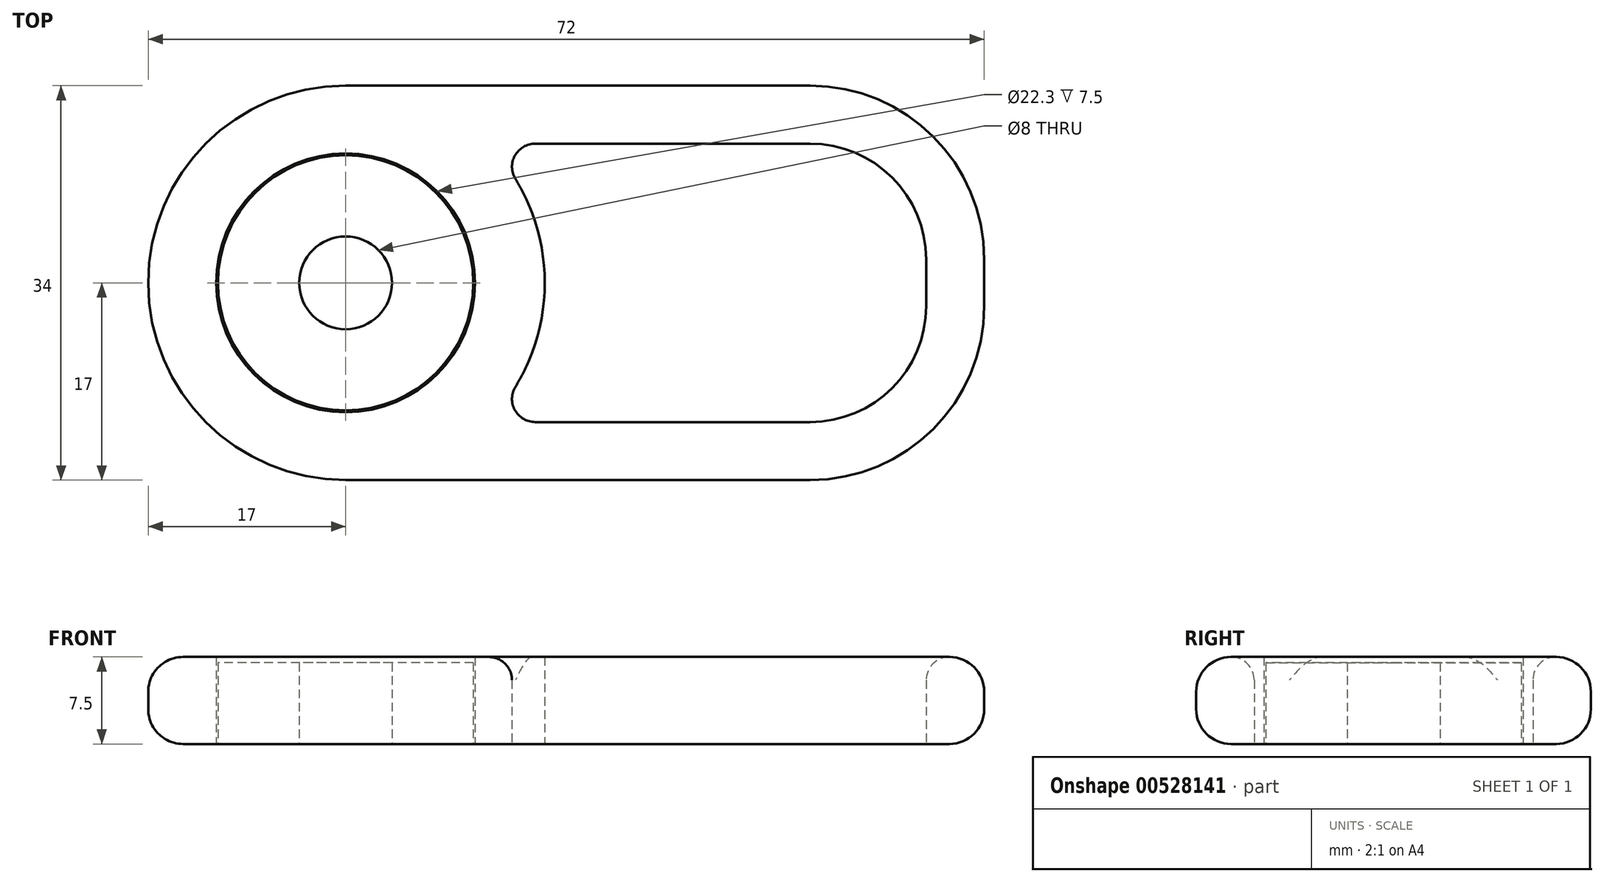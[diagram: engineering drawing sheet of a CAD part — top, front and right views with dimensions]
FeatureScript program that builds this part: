
annotation { "Feature Type Name" : "Feature", "Feature Type Description" : "" }
export const myFeature = defineFeature(function(context is Context, id is Id, definition is map)
    precondition{}
    {
        {
            var Q0;
            Q0=qCreatedBy(makeId("Top.planeOp"),FACE);
            var sketch = newSketch(context, id + "F0", { "sketchPlane" : qUnion([Q0])});
            skCircle(sketch, "E0", {"center": v(0, 0) * mm, "radius": 11 * mm});
            skCircle(sketch, "E1", {"center": v(0, 0) * mm, "radius": 4 * mm});
            skSolve(sketch);
        }
        {
            var Q0;
            Q0=makeQuery(id+"F0.imprint","IMPRINT",FACE,{"disambiguationData":[TD([[makeQuery(id+"F0.imprint","IMPRINT",EDGE,{"derivedFrom":sQuery(id+"F0.wireOp",EDGE,"E0")}),1.0]])]});
            extrude(context, id + "F1", {"entities" : qUnion([Q0]), "depth" : 7 * mm, "offsetDistance" : 25 * mm});
        }
        {
            var Q0;
            Q0=qCreatedBy(makeId("Top.planeOp"),FACE);
            var sketch = newSketch(context, id + "F2", { "sketchPlane" : qUnion([Q0])});
            skArc(sketch, "E2.0", {"start": v(0, 17) * mm, "mid": v(-17, 0) * mm, "end": v(0, -17) * mm});
            skLineSegment(sketch, "E3.bottom", {"start": v(40, -17) * mm, "end": v(0, -17) * mm});
            skLineSegment(sketch, "E3.top", {"start": v(40, 17) * mm, "end": v(0, 17) * mm});
            skLineSegment(sketch, "E3.left", {"start": v(55, -2) * mm, "end": v(55, 2) * mm});
            skPoint(sketch, "E4.visualSharp", {"position": v(55, 17) * mm});
            skArc(sketch, "E4.filletArc", {"start": v(55, 2) * mm, "mid": v(50.6, 12.6) * mm, "end": v(40, 17) * mm});
            skPoint(sketch, "E5.visualSharp", {"position": v(55, -17) * mm});
            skArc(sketch, "E5.filletArc", {"start": v(40, -17) * mm, "mid": v(50.6, -12.6) * mm, "end": v(55, -2) * mm});
            skCircle(sketch, "E6.0", {"center": v(0, 0) * mm, "radius": 11.15 * mm});
            skSolve(sketch);
        }
        {
            var Q0;
            Q0=makeQuery(id+"F2.imprint","IMPRINT",FACE,{"disambiguationData":[TD([[makeQuery(id+"F2.imprint","IMPRINT",EDGE,{"derivedFrom":sQuery(id+"F2.wireOp",EDGE,"E2.0")}),1.0]])]});
            extrude(context, id + "F3", {"entities" : qUnion([Q0]), "depth" : 7.5 * mm, "offsetDistance" : 25 * mm});
        }
        {
            var Q0;
            Q0=makeQuery(id+"F3.opExtrude","CAP_EDGE",EDGE,{"disambiguationData":[OSD([sQuery(id+"F2.wireOp",EDGE,"E3.bottom")])],"isStart":false});
            var Q1;
            Q1=makeQuery(id+"F3.opExtrude","CAP_EDGE",EDGE,{"disambiguationData":[OSD([sQuery(id+"F2.wireOp",EDGE,"E5.filletArc")])],"isStart":false});
            var Q2;
            Q2=makeQuery(id+"F3.opExtrude","CAP_EDGE",EDGE,{"disambiguationData":[OSD([sQuery(id+"F2.wireOp",EDGE,"E3.bottom")])],"isStart":true});
            fillet(context, id + "F4", {"entities" : qUnion([Q0, Q1, Q2]), "radius" : 3 * mm, "tangentPropagation" : true, "allowEdgeOverflow" : false});
        }
        {
            var Q0;
            Q0=makeQuery(id+"F3.opExtrude","CAP_FACE",FACE,{"disambiguationData":[OSD([sQuery(id+"F2.wireOp",EDGE,"E2.0"),sQuery(id+"F2.wireOp",EDGE,"E3.bottom"),sQuery(id+"F2.wireOp",EDGE,"E3.top"),sQuery(id+"F2.wireOp",EDGE,"E3.left"),sQuery(id+"F2.wireOp",EDGE,"E4.filletArc"),sQuery(id+"F2.wireOp",EDGE,"E5.filletArc"),sQuery(id+"F2.wireOp",EDGE,"E6.0")])],"isStart":true});
            var sketch = newSketch(context, id + "F5", { "sketchPlane" : qUnion([Q0])});
            skLineSegment(sketch, "E7.0", {"start": v(40, 12) * mm, "end": v(12.25, 12) * mm});
            skLineSegment(sketch, "E7.1", {"start": v(12.25, -12) * mm, "end": v(40, -12) * mm});
            skArc(sketch, "E7.2", {"start": v(40, -12) * mm, "mid": v(47.07, -9.07) * mm, "end": v(50, -2) * mm});
            skLineSegment(sketch, "E7.3", {"start": v(50, -2) * mm, "end": v(50, 2) * mm});
            skArc(sketch, "E7.4", {"start": v(50, 2) * mm, "mid": v(47.07, 9.07) * mm, "end": v(40, 12) * mm});
            skArc(sketch, "E8.0", {"start": v(12.25, -12) * mm, "mid": v(17.15, 0) * mm, "end": v(12.25, 12) * mm});
            skSolve(sketch);
        }
        {
            var Q0;
            Q0=makeQuery(id+"F5.imprint","IMPRINT",FACE,{"disambiguationData":[TD([[makeQuery(id+"F5.imprint","IMPRINT",EDGE,{"derivedFrom":sQuery(id+"F5.wireOp",EDGE,"E7.0")}),1.0]])]});
            extrude(context, id + "F6", {"entities" : qUnion([Q0]), "operationType" : NewBodyOperationType.REMOVE, "oppositeDirection" : true, "depth" : 25 * mm, "offsetDistance" : 25 * mm});
        }
        {
            var Q0;
            Q0=makeQuery(id+"F6.boolean.opBoolean","COPY",EDGE,{"derivedFrom":makeQuery(id+"F6.opExtrude","CAP_EDGE",EDGE,{"disambiguationData":[OSD([sQuery(id+"F5.wireOp",EDGE,"E7.0")])],"isStart":true})});
            var Q1;
            Q1=makeQuery(id+"F6.boolean.opBoolean","COPY",EDGE,{"derivedFrom":makeQuery(id+"F6.opExtrude","SWEPT_EDGE",EDGE,{"disambiguationData":[OSD([sQuery(id+"F5.wireOp",EDGE,"E7.0"),sQuery(id+"F5.wireOp",EDGE,"E8.0")])]})});
            var Q2;
            Q2=makeQuery(id+"F6.boolean.opBoolean","INTERSECT",EDGE,{"derivedFrom":[makeQuery(id+"F3.opExtrude","CAP_FACE",FACE,{"disambiguationData":[OSD([sQuery(id+"F2.wireOp",EDGE,"E2.0"),sQuery(id+"F2.wireOp",EDGE,"E3.bottom"),sQuery(id+"F2.wireOp",EDGE,"E3.top"),sQuery(id+"F2.wireOp",EDGE,"E3.left"),sQuery(id+"F2.wireOp",EDGE,"E4.filletArc"),sQuery(id+"F2.wireOp",EDGE,"E5.filletArc"),sQuery(id+"F2.wireOp",EDGE,"E6.0")])],"isStart":false}),makeQuery(id+"F6.opExtrude","SWEPT_FACE",FACE,{"disambiguationData":[OSD([sQuery(id+"F5.wireOp",EDGE,"E7.4")])]})]});
            var Q3;
            Q3=makeQuery(id+"F6.boolean.opBoolean","INTERSECT",EDGE,{"derivedFrom":[makeQuery(id+"F3.opExtrude","CAP_FACE",FACE,{"disambiguationData":[OSD([sQuery(id+"F2.wireOp",EDGE,"E2.0"),sQuery(id+"F2.wireOp",EDGE,"E3.bottom"),sQuery(id+"F2.wireOp",EDGE,"E3.top"),sQuery(id+"F2.wireOp",EDGE,"E3.left"),sQuery(id+"F2.wireOp",EDGE,"E4.filletArc"),sQuery(id+"F2.wireOp",EDGE,"E5.filletArc"),sQuery(id+"F2.wireOp",EDGE,"E6.0")])],"isStart":false}),makeQuery(id+"F6.opExtrude","SWEPT_FACE",FACE,{"disambiguationData":[OSD([sQuery(id+"F5.wireOp",EDGE,"E7.2")])]})]});
            var Q4;
            Q4=makeQuery(id+"F6.boolean.opBoolean","INTERSECT",EDGE,{"derivedFrom":[makeQuery(id+"F3.opExtrude","CAP_FACE",FACE,{"disambiguationData":[OSD([sQuery(id+"F2.wireOp",EDGE,"E2.0"),sQuery(id+"F2.wireOp",EDGE,"E3.bottom"),sQuery(id+"F2.wireOp",EDGE,"E3.top"),sQuery(id+"F2.wireOp",EDGE,"E3.left"),sQuery(id+"F2.wireOp",EDGE,"E4.filletArc"),sQuery(id+"F2.wireOp",EDGE,"E5.filletArc"),sQuery(id+"F2.wireOp",EDGE,"E6.0")])],"isStart":false}),makeQuery(id+"F6.opExtrude","SWEPT_FACE",FACE,{"disambiguationData":[OSD([sQuery(id+"F5.wireOp",EDGE,"E7.1")])]})]});
            var Q5;
            Q5=makeQuery(id+"F6.boolean.opBoolean","COPY",EDGE,{"derivedFrom":makeQuery(id+"F6.opExtrude","CAP_EDGE",EDGE,{"disambiguationData":[OSD([sQuery(id+"F5.wireOp",EDGE,"E7.2")])],"isStart":true})});
            var Q6;
            Q6=makeQuery(id+"F6.boolean.opBoolean","COPY",EDGE,{"derivedFrom":makeQuery(id+"F6.opExtrude","CAP_EDGE",EDGE,{"disambiguationData":[OSD([sQuery(id+"F5.wireOp",EDGE,"E7.1")])],"isStart":true})});
            var Q7;
            Q7=makeQuery(id+"F6.boolean.opBoolean","COPY",EDGE,{"derivedFrom":makeQuery(id+"F6.opExtrude","CAP_EDGE",EDGE,{"disambiguationData":[OSD([sQuery(id+"F5.wireOp",EDGE,"E7.4")])],"isStart":true})});
            var Q8;
            Q8=makeQuery(id+"F6.boolean.opBoolean","INTERSECT",EDGE,{"derivedFrom":[makeQuery(id+"F3.opExtrude","CAP_FACE",FACE,{"disambiguationData":[OSD([sQuery(id+"F2.wireOp",EDGE,"E2.0"),sQuery(id+"F2.wireOp",EDGE,"E3.bottom"),sQuery(id+"F2.wireOp",EDGE,"E3.top"),sQuery(id+"F2.wireOp",EDGE,"E3.left"),sQuery(id+"F2.wireOp",EDGE,"E4.filletArc"),sQuery(id+"F2.wireOp",EDGE,"E5.filletArc"),sQuery(id+"F2.wireOp",EDGE,"E6.0")])],"isStart":false}),makeQuery(id+"F6.opExtrude","SWEPT_FACE",FACE,{"disambiguationData":[OSD([sQuery(id+"F5.wireOp",EDGE,"E7.3")])]})]});
            var Q9;
            Q9=makeQuery(id+"F6.boolean.opBoolean","COPY",EDGE,{"derivedFrom":makeQuery(id+"F6.opExtrude","CAP_EDGE",EDGE,{"disambiguationData":[OSD([sQuery(id+"F5.wireOp",EDGE,"E7.3")])],"isStart":true})});
            var Q10;
            Q10=makeQuery(id+"F6.boolean.opBoolean","COPY",EDGE,{"derivedFrom":makeQuery(id+"F6.opExtrude","SWEPT_EDGE",EDGE,{"disambiguationData":[OSD([sQuery(id+"F5.wireOp",EDGE,"E7.1"),sQuery(id+"F5.wireOp",EDGE,"E8.0")])]})});
            fillet(context, id + "F7", {"entities" : qUnion([Q0, Q1, Q2, Q3, Q4, Q5, Q6, Q7, Q8, Q9, Q10]), "radius" : 2 * mm, "tangentPropagation" : true, "allowEdgeOverflow" : false});
        }
    });
